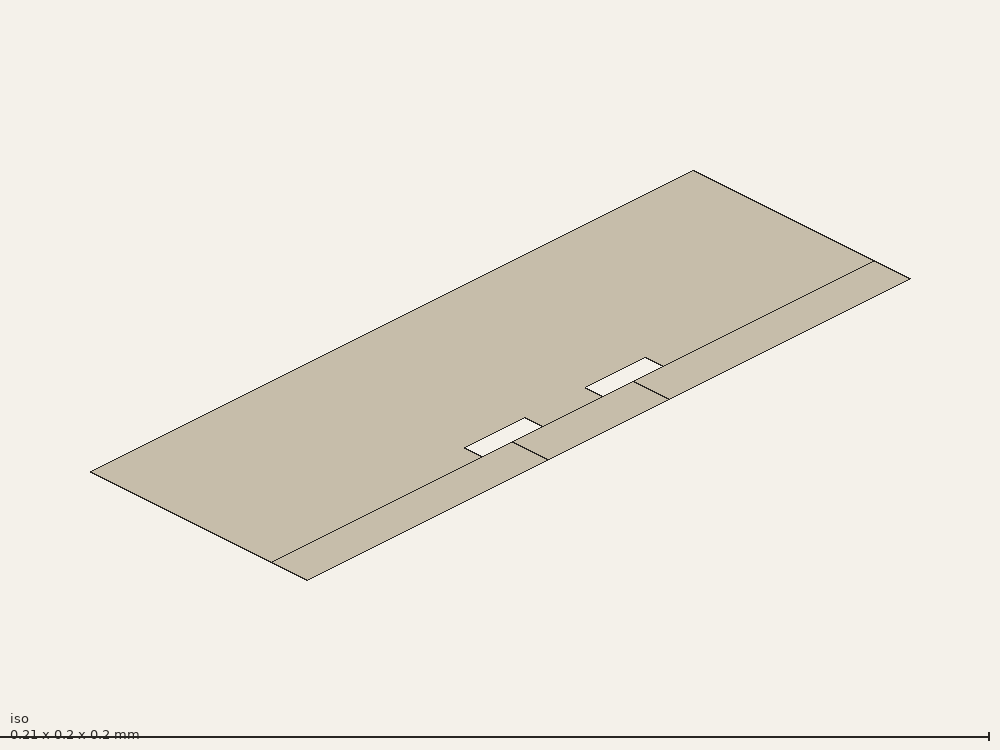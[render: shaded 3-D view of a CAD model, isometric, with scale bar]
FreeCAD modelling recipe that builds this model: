
FCSTD DOCUMENT  (FreeCAD 0.21R33694 (Git))
Label: coupled_microstrip
License: All rights reserved
LicenseURL: http://en.wikipedia.org/wiki/All_rights_reserved
objects: Part::Part2DObjectPython×8, App::FeaturePython×4, Part::Cut×2, Part::FeaturePython×1
note: 11 computed .brp shape members not serialized (recipe doc carries the construction recipe); baked Part::Feature solids carry a one-line shape summary decoded from their .brp

FEATURE [Part::Part2DObjectPython] Rectangle  label="cut1"  # Draft 2D object (typed FeaturePython)
  Area = 3e-07
  ChamferSize = 0
  Columns = 1
  FilletRadius = 0
  Height = 0.0003
  Length = 0.001
  MakeFace = true
  Placement = pos=(-0.0015,0,0) rot=(0,0,1;0rad)
  Rows = 1
FEATURE [Part::Part2DObjectPython] Rectangle001  label="_Pi1"  # Draft 2D object (typed FeaturePython)
  Area = 3e-07
  ChamferSize = 0
  Columns = 1
  FilletRadius = 0
  Height = 0.0003
  Length = 0.001
  MakeFace = true
  Placement = pos=(-0.0015,0,0) rot=(0,0,1;0rad)
  Rows = 1
FEATURE [Part::Part2DObjectPython] Rectangle002  label="cut2"  # Draft 2D object (typed FeaturePython)
  Area = 3e-07
  ChamferSize = 0
  Columns = 1
  FilletRadius = 0
  Height = 0.0003
  Length = 0.001
  MakeFace = true
  Placement = pos=(0.0005,0,0) rot=(0,0,1;0rad)
  Rows = 1
FEATURE [Part::Part2DObjectPython] Rectangle003  label="_Pi2"  # Draft 2D object (typed FeaturePython)
  Area = 3e-07
  ChamferSize = 0
  Columns = 1
  FilletRadius = 0
  Height = 0.0003
  Length = 0.001
  MakeFace = true
  Placement = pos=(0.0005,0,0) rot=(0,0,1;0rad)
  Rows = 1
FEATURE [Part::Part2DObjectPython] Rectangle004  label="substrate"  # Draft 2D object (typed FeaturePython)
  Area = 6.35e-06
  ChamferSize = 0
  Columns = 1
  FilletRadius = 0
  Height = 0.000635
  Length = 0.01
  MakeFace = true
  Placement = pos=(-0.005,-0.000635,0) rot=(0,0,1;0rad)
  Rows = 1
FEATURE [Part::Part2DObjectPython] Rectangle005  label="air"  # Draft 2D object (typed FeaturePython)
  Area = 3e-05
  ChamferSize = 0
  Columns = 1
  FilletRadius = 0
  Height = 0.003
  Length = 0.01
  MakeFace = true
  Placement = pos=(-0.005,0,0) rot=(0,0,1;0rad)
  Rows = 1
FEATURE [Part::Cut] Cut
  Base = -> Rectangle005
  Tool = -> Rectangle
FEATURE [Part::Cut] Cut001  label="air-metal"
  Base = -> Cut
  Tool = -> Rectangle002
FEATURE [Part::Part2DObjectPython] Line  label="_Pv1"  # Draft 2D object (typed FeaturePython)
  Area = 0
  ChamferSize = 0
  Closed = false
  End = (-0.001,0,0)
  FilletRadius = 0
  Length = 0.000635
  MakeFace = true
  Placement = pos=(-0.001,-0.000635,0) rot=(0,0,1;0rad)
  Points = (2) [(0,0,0),(3.88825e-20,0.000635,0)]
  Start = (-0.001,-0.000635,0)
  Subdivisions = 0
FEATURE [Part::Part2DObjectPython] Line001  label="_Pv2"  # Draft 2D object (typed FeaturePython)
  Area = 0
  ChamferSize = 0
  Closed = false
  End = (0.001,0,0)
  FilletRadius = 0
  Length = 0.000635
  MakeFace = true
  Placement = pos=(0.001,-0.000635,0) rot=(0,0,1;0rad)
  Points = (2) [(0,0,0),(3.88825e-20,0.000635,0)]
  Start = (0.001,-0.000635,0)
  Subdivisions = 0
FEATURE [App::FeaturePython] Text  label="_M1(voltage,0.5){v1,v2}"  # WARN: FeaturePython — macro-defined, semantics opaque (R4)
  Placement = pos=(-0.0314219,-0.0122714,0) rot=(0,0,1;0rad)
  Text = .
FEATURE [App::FeaturePython] Text001  label="_M2(voltage){v1,-v2}"  # WARN: FeaturePython — macro-defined, semantics opaque (R4)
  Placement = pos=(-0.0314219,-0.0122714,0) rot=(0,0,1;0rad)
  Text = .
FEATURE [App::FeaturePython] Text002  label="_M1(current){i1,i2}"  # WARN: FeaturePython — macro-defined, semantics opaque (R4)
  Placement = pos=(-0.0314219,-0.0122714,0) rot=(0,0,1;0rad)
  Text = .
FEATURE [App::FeaturePython] Text003  label="_M2(current,0.5){i1,-i2}"  # WARN: FeaturePython — macro-defined, semantics opaque (R4)
  Placement = pos=(-0.0314219,-0.0122714,0) rot=(0,0,1;0rad)
  Text = .
FEATURE [Part::FeaturePython] BooleanFragments  # WARN: FeaturePython — macro-defined, semantics opaque (R4)
  Mode = 0
  Objects = -> [Rectangle004,Cut001,Line,Line001]
  Tolerance = 0
